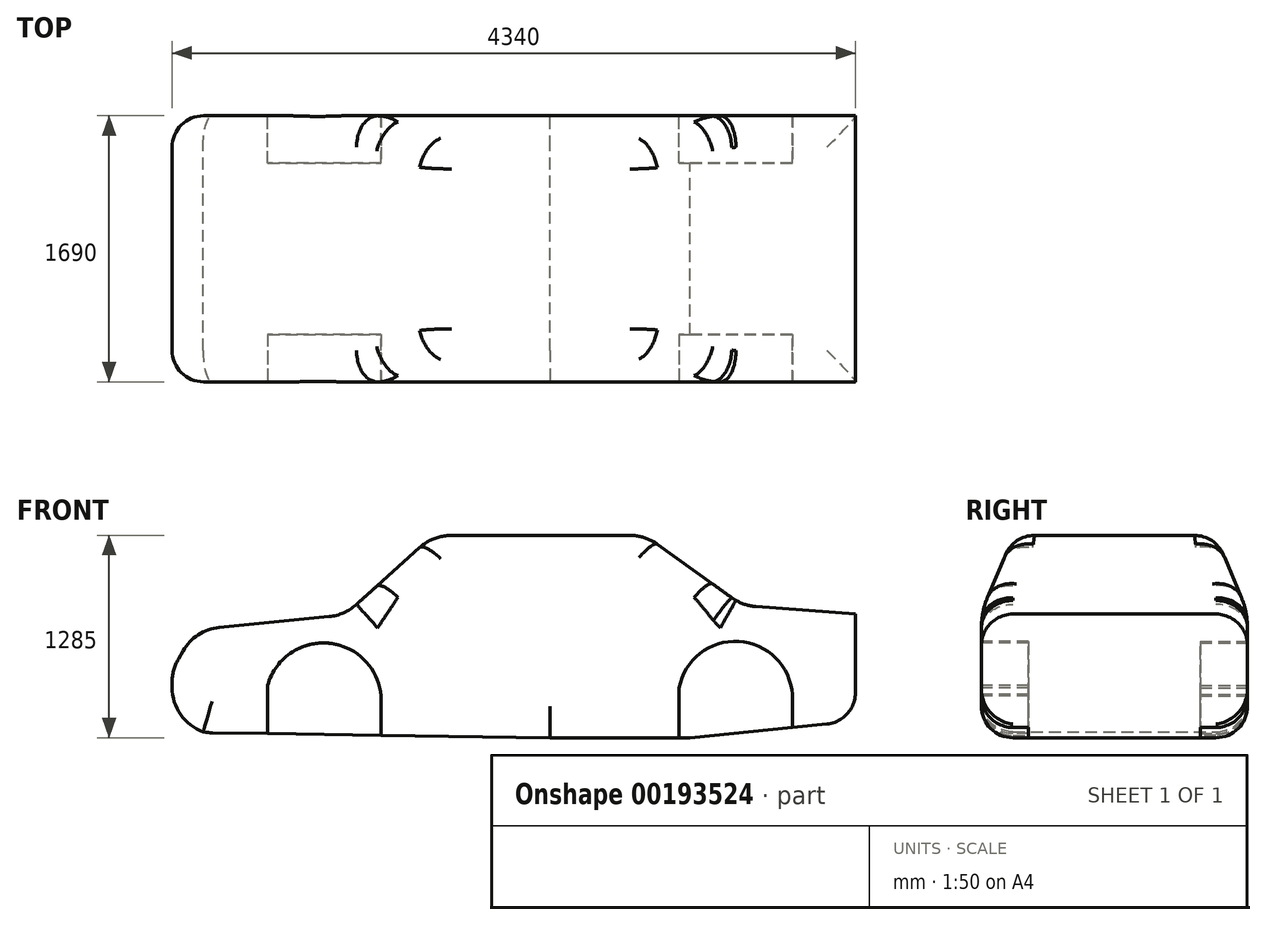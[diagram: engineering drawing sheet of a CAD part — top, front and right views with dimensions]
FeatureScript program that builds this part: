
annotation { "Feature Type Name" : "Feature", "Feature Type Description" : "" }
export const myFeature = defineFeature(function(context is Context, id is Id, definition is map)
    precondition{}
    {
        {
            var Q0;
            Q0=qCreatedBy(makeId("Front.planeOp"),FACE);
            var sketch = newSketch(context, id + "F0", { "sketchPlane" : qUnion([Q0])});
            skLineSegment(sketch, "E0", {"start": v(0, 115) * mm, "end": v(889.28, 115) * mm});
            skLineSegment(sketch, "E1", {"start": v(889.28, 115) * mm, "end": v(1940, 219.8) * mm});
            skLineSegment(sketch, "E2", {"start": v(1940, 219.8) * mm, "end": v(1940, 900) * mm});
            skLineSegment(sketch, "E3", {"start": v(1940, 900) * mm, "end": v(1223.34, 954.39) * mm});
            skLineSegment(sketch, "E4", {"start": v(1223.34, 954.39) * mm, "end": v(604.14, 1400) * mm});
            skLineSegment(sketch, "E5", {"start": v(604.14, 1400) * mm, "end": v(-741.84, 1400) * mm});
            skLineSegment(sketch, "E6", {"start": v(-741.84, 1400) * mm, "end": v(-1303.94, 893.7) * mm});
            skLineSegment(sketch, "E7", {"start": v(-1303.94, 893.7) * mm, "end": v(-2254.03, 800) * mm});
            skLineSegment(sketch, "E8", {"start": v(-2254.03, 800) * mm, "end": v(-2400, 545.5) * mm});
            skLineSegment(sketch, "E9", {"start": v(-2400, 545.5) * mm, "end": v(-2400, 209.32) * mm});
            skLineSegment(sketch, "E10", {"start": v(-2400, 209.32) * mm, "end": v(-2183.5, 146.47) * mm});
            skLineSegment(sketch, "E11", {"start": v(-2183.5, 146.47) * mm, "end": v(0, 115) * mm});
            skSolve(sketch);
        }
        {
            var Q0;
            Q0=makeQuery(id+"F0.imprint","IMPRINT",FACE,{"disambiguationData":[TD([[makeQuery(id+"F0.imprint","IMPRINT",EDGE,{"derivedFrom":sQuery(id+"F0.wireOp",EDGE,"E0")}),1.0]])]});
            extrude(context, id + "F1", {"entities" : qUnion([Q0]), "depth" : (1690 / 2) * mm});
        }
        {
            var Q0;
            Q0=qCreatedBy(makeId("Right.planeOp"),FACE);
            var sketch = newSketch(context, id + "F2", { "sketchPlane" : qUnion([Q0])});
            skLineSegment(sketch, "E12", {"start": v(-604.14, 1487.1) * mm, "end": v(-885.4, 817.59) * mm});
            skLineSegment(sketch, "E13", {"start": v(-885.4, 817.59) * mm, "end": v(-885.4, 1493.21) * mm});
            skLineSegment(sketch, "E14", {"start": v(-885.4, 1493.21) * mm, "end": v(-604.14, 1487.1) * mm});
            skSolve(sketch);
        }
        {
            var Q0;
            Q0 = qSketchRegion(id + "F2", true);
            extrude(context, id + "F3", {"entities" : qUnion([Q0]), "operationType" : NewBodyOperationType.REMOVE, "endBound" : BoundingType.THROUGH_ALL, "oppositeDirection" : true, "depth" : 25 * mm, "hasSecondDirection" : true, "secondDirectionBound" : SecondDirectionBoundingType.THROUGH_ALL, "secondDirectionOppositeDirection" : false, "secondDirectionDepth" : 25 * mm});
        }
        {
            var Q0;
            Q0=makeQuery(id+"F1.opExtrude","SWEPT_EDGE",EDGE,{"disambiguationData":[OSD([sQuery(id+"F0.wireOp",EDGE,"E5"),sQuery(id+"F0.wireOp",EDGE,"E6")])]});
            var Q1;
            Q1=makeQuery(id+"F1.opExtrude","SWEPT_EDGE",EDGE,{"disambiguationData":[OSD([sQuery(id+"F0.wireOp",EDGE,"E4"),sQuery(id+"F0.wireOp",EDGE,"E5")])]});
            var Q2;
            Q2=makeQuery(id+"F1.opExtrude","SWEPT_EDGE",EDGE,{"disambiguationData":[OSD([sQuery(id+"F0.wireOp",EDGE,"E6"),sQuery(id+"F0.wireOp",EDGE,"E7")])]});
            var Q3;
            Q3=makeQuery(id+"F1.opExtrude","SWEPT_EDGE",EDGE,{"disambiguationData":[OSD([sQuery(id+"F0.wireOp",EDGE,"E3"),sQuery(id+"F0.wireOp",EDGE,"E4")])]});
            fillet(context, id + "F4", {"entities" : qUnion([Q0, Q1, Q2, Q3]), "radius" : 300 * mm, "tangentPropagation" : true, "allowEdgeOverflow" : false});
        }
        {
            var Q0;
            Q0=makeQuery(id+"F3.boolean.opBoolean","INTERSECT",EDGE,{"derivedFrom":[makeQuery(id+"F1.opExtrude","CAP_FACE",FACE,{"disambiguationData":[OSD([sQuery(id+"F0.wireOp",EDGE,"E0"),sQuery(id+"F0.wireOp",EDGE,"E1"),sQuery(id+"F0.wireOp",EDGE,"E2"),sQuery(id+"F0.wireOp",EDGE,"E3"),sQuery(id+"F0.wireOp",EDGE,"E4"),sQuery(id+"F0.wireOp",EDGE,"E5"),sQuery(id+"F0.wireOp",EDGE,"E6"),sQuery(id+"F0.wireOp",EDGE,"E7"),sQuery(id+"F0.wireOp",EDGE,"E8"),sQuery(id+"F0.wireOp",EDGE,"E9"),sQuery(id+"F0.wireOp",EDGE,"E10"),sQuery(id+"F0.wireOp",EDGE,"E11")])],"isStart":false}),makeQuery(id+"F3.opExtrude","SWEPT_FACE",FACE,{"disambiguationData":[OSD([sQuery(id+"F2.wireOp",EDGE,"E12")])]})]});
            fillet(context, id + "F5", {"entities" : qUnion([Q0]), "radius" : 500 * mm, "tangentPropagation" : true, "allowEdgeOverflow" : false});
        }
        {
            var Q0;
            Q0=makeQuery(id+"F1.opExtrude","SWEPT_EDGE",EDGE,{"disambiguationData":[OSD([sQuery(id+"F0.wireOp",EDGE,"E7"),sQuery(id+"F0.wireOp",EDGE,"E8")])]});
            var Q1;
            Q1=makeQuery(id+"F1.opExtrude","SWEPT_EDGE",EDGE,{"disambiguationData":[OSD([sQuery(id+"F0.wireOp",EDGE,"E8"),sQuery(id+"F0.wireOp",EDGE,"E9")])]});
            var Q2;
            Q2=makeQuery(id+"F1.opExtrude","SWEPT_EDGE",EDGE,{"disambiguationData":[OSD([sQuery(id+"F0.wireOp",EDGE,"E9"),sQuery(id+"F0.wireOp",EDGE,"E10")])]});
            var Q3;
            Q3=makeQuery(id+"F1.opExtrude","SWEPT_EDGE",EDGE,{"disambiguationData":[OSD([sQuery(id+"F0.wireOp",EDGE,"E10"),sQuery(id+"F0.wireOp",EDGE,"E11")])]});
            fillet(context, id + "F6", {"entities" : qUnion([Q0, Q1, Q2, Q3]), "radius" : 300 * mm, "tangentPropagation" : true, "allowEdgeOverflow" : false});
        }
        {
            var Q0;
            Q0=makeQuery(id+"F1.opExtrude","CAP_EDGE",EDGE,{"disambiguationData":[OSD([sQuery(id+"F0.wireOp",EDGE,"E1")])],"isStart":false});
            var Q1;
            Q1=makeQuery(id+"F1.opExtrude","SWEPT_EDGE",EDGE,{"disambiguationData":[OSD([sQuery(id+"F0.wireOp",EDGE,"E1"),sQuery(id+"F0.wireOp",EDGE,"E2")])]});
            var Q2;
            Q2=makeQuery(id+"F1.opExtrude","CAP_EDGE",EDGE,{"disambiguationData":[OSD([sQuery(id+"F0.wireOp",EDGE,"E11")])],"isStart":false});
            var Q3;
            Q3=makeQuery(id+"F1.opExtrude","CAP_EDGE",EDGE,{"disambiguationData":[OSD([sQuery(id+"F0.wireOp",EDGE,"E0")])],"isStart":false});
            var Q4;
            {var subQ0=sQuery(id+"F0.wireOp",EDGE,"E7");Q4=makeQuery(id+"F5.opFillet","BLEND_EDGE",EDGE,{"blendedFrom":[makeQuery(id+"F3.boolean.opBoolean","INTERSECT",EDGE,{"derivedFrom":[makeQuery(id+"F1.opExtrude","CAP_FACE",FACE,{"disambiguationData":[OSD([sQuery(id+"F0.wireOp",EDGE,"E0"),sQuery(id+"F0.wireOp",EDGE,"E1"),sQuery(id+"F0.wireOp",EDGE,"E2"),sQuery(id+"F0.wireOp",EDGE,"E3"),sQuery(id+"F0.wireOp",EDGE,"E4"),sQuery(id+"F0.wireOp",EDGE,"E5"),sQuery(id+"F0.wireOp",EDGE,"E6"),subQ0,sQuery(id+"F0.wireOp",EDGE,"E8"),sQuery(id+"F0.wireOp",EDGE,"E9"),sQuery(id+"F0.wireOp",EDGE,"E10"),sQuery(id+"F0.wireOp",EDGE,"E11")])],"isStart":false}),makeQuery(id+"F3.opExtrude","SWEPT_FACE",FACE,{"disambiguationData":[OSD([sQuery(id+"F2.wireOp",EDGE,"E12")])]})]}),makeQuery(id+"F1.opExtrude","SWEPT_FACE",FACE,{"disambiguationData":[OSD([subQ0])]})],"blendedInto":[makeQuery(id+"F1.opExtrude","SWEPT_FACE",FACE,{"disambiguationData":[OSD([subQ0])]})]});}
            fillet(context, id + "F7", {"entities" : qUnion([Q0, Q1, Q2, Q3, Q4]), "radius" : 200 * mm, "tangentPropagation" : true, "allowEdgeOverflow" : false});
        }
        {
            var Q0;
            Q0=makeQuery(id+"F1.opExtrude","CAP_FACE",FACE,{"disambiguationData":[OSD([sQuery(id+"F0.wireOp",EDGE,"E0"),sQuery(id+"F0.wireOp",EDGE,"E1"),sQuery(id+"F0.wireOp",EDGE,"E2"),sQuery(id+"F0.wireOp",EDGE,"E3"),sQuery(id+"F0.wireOp",EDGE,"E4"),sQuery(id+"F0.wireOp",EDGE,"E5"),sQuery(id+"F0.wireOp",EDGE,"E6"),sQuery(id+"F0.wireOp",EDGE,"E7"),sQuery(id+"F0.wireOp",EDGE,"E8"),sQuery(id+"F0.wireOp",EDGE,"E9"),sQuery(id+"F0.wireOp",EDGE,"E10"),sQuery(id+"F0.wireOp",EDGE,"E11")])],"isStart":false});
            var sketch = newSketch(context, id + "F8", { "sketchPlane" : qUnion([Q0])});
            skLineSegment(sketch, "E15", {"start": v(-1793.47, 447.9) * mm, "end": v(-1793.47, 0) * mm});
            skLineSegment(sketch, "E16", {"start": v(-1793.47, 0) * mm, "end": v(-1073.47, 0) * mm});
            skLineSegment(sketch, "E17", {"start": v(-1073.47, 0) * mm, "end": v(-1073.47, 381.73) * mm});
            skArc(sketch, "E18", {"start": v(-1073.47, 381.73) * mm, "mid": v(-1405.86, 715.2) * mm, "end": v(-1793.47, 447.9) * mm});
            skLineSegment(sketch, "E19", {"start": v(819.81, 429.76) * mm, "end": v(819.81, 0) * mm});
            skLineSegment(sketch, "E20", {"start": v(819.81, 0) * mm, "end": v(1539.81, 0) * mm});
            skLineSegment(sketch, "E21", {"start": v(1539.81, 0) * mm, "end": v(1539.81, 388.47) * mm});
            skArc(sketch, "E22", {"start": v(1539.81, 388.47) * mm, "mid": v(1198.01, 726.48) * mm, "end": v(819.81, 429.76) * mm});
            skSolve(sketch);
        }
        {
            var Q0;
            Q0 = qSketchRegion(id + "F8", true);
            extrude(context, id + "F9", {"entities" : qUnion([Q0]), "operationType" : NewBodyOperationType.REMOVE, "oppositeDirection" : true, "depth" : 300 * mm});
        }
        {
            var Q0;
            Q0=makeQuery(id+"F1.opExtrude","SWEPT_BODY",BODY,{"disambiguationData":[OSD([sQuery(id+"F0.wireOp",EDGE,"E0"),sQuery(id+"F0.wireOp",EDGE,"E1"),sQuery(id+"F0.wireOp",EDGE,"E2"),sQuery(id+"F0.wireOp",EDGE,"E3"),sQuery(id+"F0.wireOp",EDGE,"E4"),sQuery(id+"F0.wireOp",EDGE,"E5"),sQuery(id+"F0.wireOp",EDGE,"E6"),sQuery(id+"F0.wireOp",EDGE,"E7"),sQuery(id+"F0.wireOp",EDGE,"E8"),sQuery(id+"F0.wireOp",EDGE,"E9"),sQuery(id+"F0.wireOp",EDGE,"E10"),sQuery(id+"F0.wireOp",EDGE,"E11")])]});
            var Q1;
            Q1=makeQuery(id+"F1.opExtrude","CAP_FACE",FACE,{"disambiguationData":[OSD([sQuery(id+"F0.wireOp",EDGE,"E0"),sQuery(id+"F0.wireOp",EDGE,"E1"),sQuery(id+"F0.wireOp",EDGE,"E2"),sQuery(id+"F0.wireOp",EDGE,"E3"),sQuery(id+"F0.wireOp",EDGE,"E4"),sQuery(id+"F0.wireOp",EDGE,"E5"),sQuery(id+"F0.wireOp",EDGE,"E6"),sQuery(id+"F0.wireOp",EDGE,"E7"),sQuery(id+"F0.wireOp",EDGE,"E8"),sQuery(id+"F0.wireOp",EDGE,"E9"),sQuery(id+"F0.wireOp",EDGE,"E10"),sQuery(id+"F0.wireOp",EDGE,"E11")])],"isStart":true});
            mirror(context, id + "F10", {"operationType" : NewBodyOperationType.ADD, "entities" : qUnion([Q0]), "mirrorPlane" : qUnion([Q1])});
        }
    });
